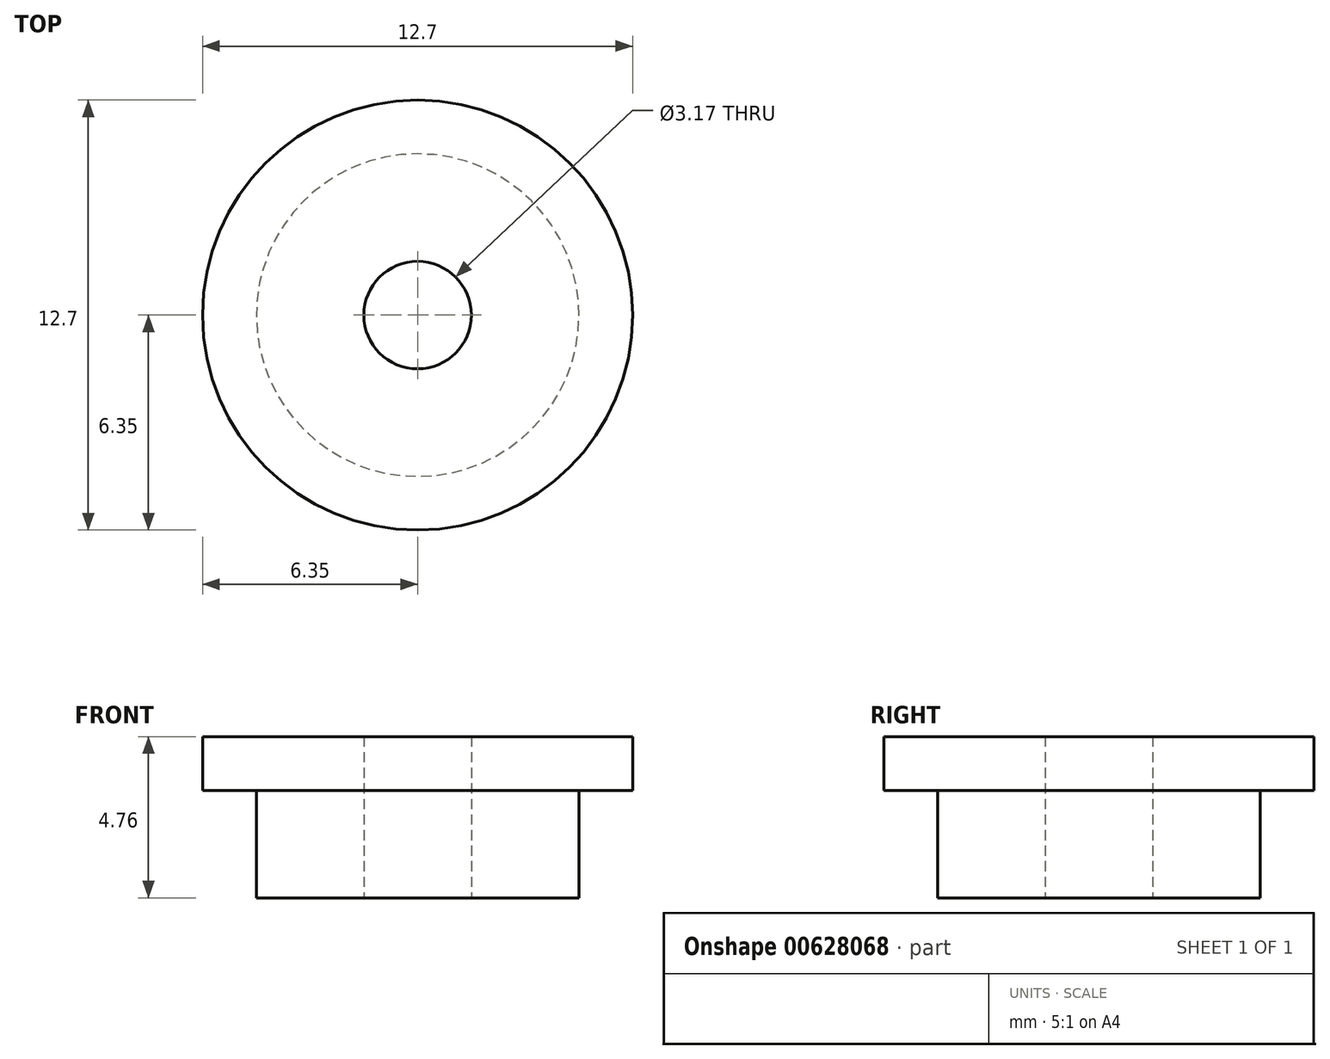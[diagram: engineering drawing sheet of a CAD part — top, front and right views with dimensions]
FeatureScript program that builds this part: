
annotation { "Feature Type Name" : "Feature", "Feature Type Description" : "" }
export const myFeature = defineFeature(function(context is Context, id is Id, definition is map)
    precondition{}
    {
        {
            var Q0;
            Q0=qCreatedBy(makeId("Front.planeOp"),FACE);
            var sketch = newSketch(context, id + "F0", { "sketchPlane" : qUnion([Q0])});
            skLineSegment(sketch, "E0", {"start": v(1.59, 0) * mm, "end": v(1.59, 4.76) * mm});
            skLineSegment(sketch, "E1", {"start": v(1.59, 4.76) * mm, "end": v(6.35, 4.76) * mm});
            skLineSegment(sketch, "E2", {"start": v(6.35, 4.76) * mm, "end": v(6.35, 3.18) * mm});
            skLineSegment(sketch, "E3", {"start": v(6.35, 3.18) * mm, "end": v(4.76, 3.18) * mm});
            skLineSegment(sketch, "E4", {"start": v(4.76, 3.18) * mm, "end": v(4.76, 0) * mm});
            skLineSegment(sketch, "E5", {"start": v(4.76, 0) * mm, "end": v(1.59, 0) * mm});
            skLineSegment(sketch, "E6", {"start": v(0, 0) * mm, "end": v(0, 6.48) * mm, "construction": true});
            skSolve(sketch);
        }
        {
            var Q0;
            Q0=makeQuery(id+"F0.imprint","IMPRINT",FACE,{"disambiguationData":[TD([[makeQuery(id+"F0.imprint","IMPRINT",EDGE,{"derivedFrom":sQuery(id+"F0.wireOp",EDGE,"E0")}),-1.0]])]});
            var Q1;
            Q1=sQuery(id+"F0.wireOp",EDGE,"E6");
            revolve(context, id + "F1", {"entities" : qUnion([Q0]), "axis" : qUnion([Q1]), "revolveType" : RevolveType.FULL});
        }
    });
